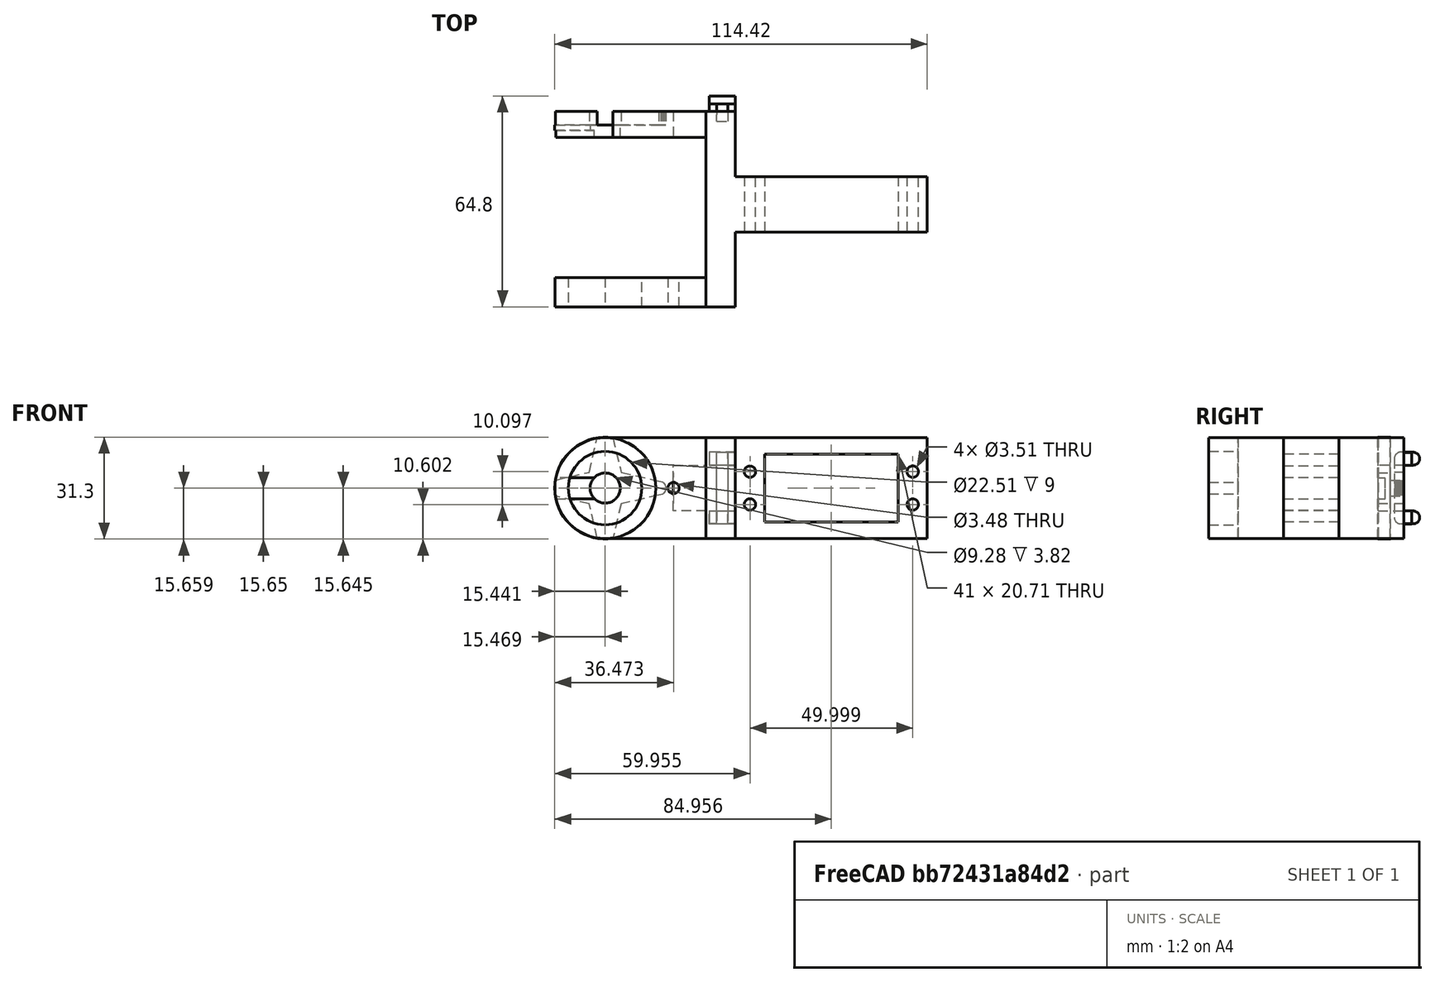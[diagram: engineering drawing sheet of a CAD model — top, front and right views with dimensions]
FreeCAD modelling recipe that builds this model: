
FCSTD DOCUMENT  (FreeCAD 1.0R38806 (Git))
Label: Eslabon_ajolote
License: All rights reserved
LicenseURL: https://en.wikipedia.org/wiki/All_rights_reserved
objects: Sketcher::SketchObject×17, TechDraw::DrawViewDimension×14, PartDesign::Pad×8, PartDesign::Pocket×8, PartDesign::Body×5, TechDraw::DrawProjGroupItem×5, PartDesign::ShapeBinder×4, PartDesign::Fillet×3, Part::MultiFuse×2, Part::Extrusion×1, Part::Fillet×1, TechDraw::DrawSVGTemplate×1, TechDraw::DrawProjGroup×1, TechDraw::DrawPage×1
note: 118 computed .brp shape members not serialized (recipe doc carries the construction recipe); baked Part::Feature solids carry a one-line shape summary decoded from their .brp

FEATURE [Sketcher::SketchObject] Sketch  label="rectángulo_atrás"
  ArcFitTolerance = 1e-06
  AttachmentSupport = -> [XY_Plane]
  FullyConstrained = false
  MakeInternals = false
  MapMode = 5
  sketch-geometry (4):
    g0: LineSegment StartX=94.9599 StartY=-16.0075 StartZ=0 EndX=35.9999 EndY=-16.0075 EndZ=0
    g1: LineSegment StartX=35.9999 StartY=-16.0075 StartZ=0 EndX=35.9999 EndY=-32.9967 EndZ=0
    g2: LineSegment StartX=35.9999 StartY=-32.9967 StartZ=0 EndX=94.9599 EndY=-32.9967 EndZ=0
    g3: LineSegment StartX=94.9599 StartY=-32.9967 StartZ=0 EndX=94.9599 EndY=-16.0075 EndZ=0
  constraints (8):
    c: Coincident(g0,g1)
    c: Coincident(g1,g2)
    c: Coincident(g2,g3)
    c: Coincident(g3,g0)
    c: Horizontal(g0)
    c: Horizontal(g2)
    c: Vertical(g1)
    c: Vertical(g3)
FEATURE [PartDesign::Pad] Pad  label="rectangulo_atras_extrusion"
  Direction = (0,0,1)
  Length = 31
  Length2 = 10
  Midplane = true
  Profile = -> Sketch
  ReferenceAxis = -> Sketch [N_Axis]
  Refine = true
  Suppressed = false
  Type = 0
FEATURE [Sketcher::SketchObject] Sketch001  label="orificios_parte_trasera"
  ArcFitTolerance = 1e-06
  AttachmentSupport = -> [Pad]
  FullyConstrained = false
  MakeInternals = false
  MapMode = 5
  Placement = pos=(0,-16.0075,0) rot=(0,0.707107,0.707107;3.14159rad)
  sketch-geometry (8):
    g0: LineSegment StartX=-85.9937 StartY=10.3574 StartZ=0 EndX=-85.9937 EndY=-10.3571 EndZ=0
    g1: LineSegment StartX=-85.9937 StartY=-10.3571 StartZ=0 EndX=-44.998 EndY=-10.3571 EndZ=0
    g2: LineSegment StartX=-44.998 StartY=-10.3571 StartZ=0 EndX=-44.998 EndY=10.3574 EndZ=0
    g3: LineSegment StartX=-44.998 StartY=10.3574 StartZ=0 EndX=-85.9937 EndY=10.3574 EndZ=0
    g4: Circle CenterX=-90.4933 CenterY=5.04829 CenterZ=0 NormalX=0 NormalY=0 NormalZ=1 AngleXU=0 Radius=1.75468
    g5: Circle CenterX=-90.4933 CenterY=-5.04829 CenterZ=0 NormalX=0 NormalY=0 NormalZ=1 AngleXU=0 Radius=1.75468
    g6: Circle CenterX=-40.4945 CenterY=5.04068 CenterZ=0 NormalX=0 NormalY=0 NormalZ=1 AngleXU=0 Radius=1.75279
    g7: Circle CenterX=-40.4945 CenterY=-5.04068 CenterZ=0 NormalX=0 NormalY=0 NormalZ=1 AngleXU=0 Radius=1.75279
  constraints (8):
    c: Coincident(g0,g1)
    c: Coincident(g1,g2)
    c: Coincident(g2,g3)
    c: Coincident(g3,g0)
    c: Vertical(g0)
    c: Vertical(g2)
    c: Horizontal(g1)
    c: Horizontal(g3)
FEATURE [PartDesign::Pocket] Pocket  label="rectangulo_atras_orificios"
  BaseFeature = -> Pad
  Direction = (0,-1,2e-16)
  Length = 4
  Length2 = 5
  Profile = -> Sketch001
  ReferenceAxis = -> Sketch001 [N_Axis]
  Refine = true
  Suppressed = false
  Type = 1
FEATURE [PartDesign::Body] Body  label="rectaángulo_de_atrás"
  AllowCompound = false
  Group = -> [Sketch,Pad,Sketch001,Pocket]
  Origin = -> Origin
  Tip = -> Pocket
FEATURE [Sketcher::SketchObject] Sketch002  label="rectangulo_vertical"
  ArcFitTolerance = 1e-06
  AttachmentSupport = -> [XY_Plane001]
  FullyConstrained = false
  MakeInternals = false
  MapMode = 5
  sketch-geometry (4):
    g0: LineSegment StartX=36 StartY=4 StartZ=0 EndX=27.0221 EndY=4 EndZ=0
    g1: LineSegment StartX=27.0221 StartY=4 StartZ=0 EndX=27.0221 EndY=-55.9831 EndZ=0
    g2: LineSegment StartX=27.0221 StartY=-55.9831 StartZ=0 EndX=36 EndY=-55.9831 EndZ=0
    g3: LineSegment StartX=36 StartY=-55.9831 StartZ=0 EndX=36 EndY=4 EndZ=0
  constraints (8):
    c: Coincident(g0,g1)
    c: Coincident(g1,g2)
    c: Coincident(g2,g3)
    c: Coincident(g3,g0)
    c: Horizontal(g0)
    c: Horizontal(g2)
    c: Vertical(g1)
    c: Vertical(g3)
FEATURE [PartDesign::Pad] Pad001
  Direction = (0,0,1)
  Length = 31
  Length2 = 10
  Midplane = true
  Profile = -> Sketch002
  ReferenceAxis = -> Sketch002 [N_Axis]
  Refine = true
  Suppressed = false
  Type = 0
FEATURE [Sketcher::SketchObject] Sketch003
  ArcFitTolerance = 1e-06
  AttachmentSupport = -> [Pad001]
  FullyConstrained = false
  MakeInternals = false
  MapMode = 5
  Placement = pos=(0,4,0) rot=(0,0.707107,0.707107;3.14159rad)
  sketch-geometry (4):
    g0: LineSegment StartX=-33.7559 StartY=-11.0015 StartZ=0 EndX=-30.2635 EndY=-11.0015 EndZ=0
    g1: LineSegment StartX=-30.2635 StartY=-11.0015 StartZ=0 EndX=-30.2635 EndY=11.0197 EndZ=0
    g2: LineSegment StartX=-30.2635 StartY=11.0197 StartZ=0 EndX=-33.7559 EndY=11.0197 EndZ=0
    g3: LineSegment StartX=-33.7559 StartY=11.0197 StartZ=0 EndX=-33.7559 EndY=-11.0015 EndZ=0
  constraints (8):
    c: Coincident(g0,g1)
    c: Coincident(g1,g2)
    c: Coincident(g2,g3)
    c: Coincident(g3,g0)
    c: Horizontal(g0)
    c: Horizontal(g2)
    c: Vertical(g1)
    c: Vertical(g3)
FEATURE [PartDesign::Pocket] Pocket001
  BaseFeature = -> Pad001
  Direction = (0,-1,2e-16)
  Length = 3
  Length2 = 5
  Profile = -> Sketch003
  ReferenceAxis = -> Sketch003 [N_Axis]
  Refine = true
  Suppressed = false
  Type = 0
FEATURE [PartDesign::Fillet] Fillet
  Base = -> Pocket001 [Edge24]
  BaseFeature = -> Pocket001
  Radius = 2
  Refine = true
  SupportTransform = false
  Suppressed = false
  UseAllEdges = false
FEATURE [PartDesign::Fillet] Fillet001
  Base = -> Fillet [Edge18]
  BaseFeature = -> Fillet
  Radius = 2
  Refine = true
  SupportTransform = false
  Suppressed = false
  UseAllEdges = false
FEATURE [Sketcher::SketchObject] Sketch004  label="base_arcos"
  ArcFitTolerance = 1e-06
  AttachmentSupport = -> [Fillet001]
  FullyConstrained = false
  MakeInternals = false
  MapMode = 5
  Placement = pos=(0,4,0) rot=(0,0.707107,0.707107;3.14159rad)
  sketch-geometry (16):
    g0: LineSegment StartX=-36.0015 StartY=-7.01539 StartZ=0 EndX=-36.0015 EndY=-10.9602 EndZ=0
    g1: LineSegment StartX=-36.0015 StartY=-10.9602 StartZ=0 EndX=-33.7554 EndY=-10.9602 EndZ=0
    g2: LineSegment StartX=-33.7554 StartY=-10.9602 StartZ=0 EndX=-33.7554 EndY=-7.01539 EndZ=0
    g3: LineSegment StartX=-33.7554 StartY=-7.01539 StartZ=0 EndX=-36.0015 EndY=-7.01539 EndZ=0
    g4: LineSegment StartX=-30.262 StartY=-10.9898 StartZ=0 EndX=-28.0069 EndY=-10.9898 EndZ=0
    g5: LineSegment StartX=-28.0069 StartY=-10.9898 StartZ=0 EndX=-28.0069 EndY=-7.03972 EndZ=0
    g6: LineSegment StartX=-28.0069 StartY=-7.03972 StartZ=0 EndX=-30.262 EndY=-7.03972 EndZ=0
    g7: LineSegment StartX=-30.262 StartY=-7.03972 StartZ=0 EndX=-30.262 EndY=-10.9898 EndZ=0
    g8: LineSegment StartX=-33.7554 StartY=7.01539 StartZ=0 EndX=-36.0015 EndY=7.01539 EndZ=0
    g9: LineSegment StartX=-36.0015 StartY=7.01539 StartZ=0 EndX=-36.0015 EndY=10.9602 EndZ=0
    g10: LineSegment StartX=-33.7554 StartY=10.9602 StartZ=0 EndX=-33.7554 EndY=7.01539 EndZ=0
    g11: LineSegment StartX=-36.0015 StartY=10.9602 StartZ=0 EndX=-33.7554 EndY=10.9602 EndZ=0
    g12: LineSegment StartX=-30.262 StartY=7.03972 StartZ=0 EndX=-30.262 EndY=10.9898 EndZ=0
    g13: LineSegment StartX=-30.262 StartY=10.9898 StartZ=0 EndX=-28.0069 EndY=10.9898 EndZ=0
    g14: LineSegment StartX=-28.0069 StartY=10.9898 StartZ=0 EndX=-28.0069 EndY=7.03972 EndZ=0
    g15: LineSegment StartX=-28.0069 StartY=7.03972 StartZ=0 EndX=-30.262 EndY=7.03972 EndZ=0
  constraints (32):
    c: Coincident(g0,g1)
    c: Coincident(g1,g2)
    c: Coincident(g2,g3)
    c: Coincident(g3,g0)
    c: Vertical(g0)
    c: Vertical(g2)
    c: Horizontal(g1)
    c: Horizontal(g3)
    c: Coincident(g4,g5)
    c: Coincident(g5,g6)
    c: Coincident(g6,g7)
    c: Coincident(g7,g4)
    c: Horizontal(g4)
    c: Horizontal(g6)
    c: Vertical(g5)
    c: Vertical(g7)
    c: Coincident(g9,g11)
    c: Coincident(g11,g10)
    c: Coincident(g10,g8)
    c: Coincident(g8,g9)
    c: Vertical(g9)
    c: Vertical(g10)
    c: Horizontal(g11)
    c: Horizontal(g8)
    c: Coincident(g13,g14)
    c: Coincident(g14,g15)
    c: Coincident(g15,g12)
    c: Coincident(g12,g13)
    c: Horizontal(g13)
    c: Horizontal(g15)
    c: Vertical(g14)
    c: Vertical(g12)
FEATURE [PartDesign::Pad] Pad002
  BaseFeature = -> Fillet001
  Direction = (0,1,-2e-16)
  Length = 2.3
  Length2 = 10
  Profile = -> Sketch004
  ReferenceAxis = -> Sketch004 [N_Axis]
  Refine = true
  Suppressed = false
  Type = 0
FEATURE [PartDesign::Body] Body001  label="rectángulo_vertical"
  AllowCompound = false
  Group = -> [Sketch002,Pad001,Sketch003,Pocket001,Fillet,Fillet001,Sketch004,Pad002]
  Origin = -> Origin001
  Tip = -> Pad002
FEATURE [PartDesign::ShapeBinder] CopyPad002
  TraceSupport = false
FEATURE [Sketcher::SketchObject] Sketch005  label="arco1"
  ArcFitTolerance = 1e-06
  AttachmentSupport = -> [CopyPad002]
  FullyConstrained = false
  MakeInternals = false
  MapMode = 5
  Placement = pos=(28.0069,0,0) rot=(0.57735,-0.57735,-0.57735;2.0944rad)
  sketch-geometry (4):
    g0: LineSegment StartX=-6.29983 StartY=-10.98 StartZ=0 EndX=-6.29983 EndY=-7.03975 EndZ=0
    g1: LineSegment StartX=-6.29983 StartY=-7.03975 StartZ=0 EndX=-8.80088 EndY=-7.03975 EndZ=0
    g2: LineSegment StartX=-8.80088 StartY=-7.03975 StartZ=0 EndX=-8.80088 EndY=-10.98 EndZ=0
    g3: LineSegment StartX=-8.80088 StartY=-10.98 StartZ=0 EndX=-6.29983 EndY=-10.98 EndZ=0
  constraints (8):
    c: Coincident(g1,g2)
    c: Coincident(g2,g3)
    c: Coincident(g3,g0)
    c: Coincident(g0,g1)
    c: Horizontal(g1)
    c: Horizontal(g3)
    c: Vertical(g2)
    c: Vertical(g0)
FEATURE [PartDesign::Pad] Pad003
  Direction = (-1,0,0)
  Length = 8
  Length2 = 10
  Profile = -> Sketch005
  ReferenceAxis = -> Sketch005 [N_Axis]
  Refine = true
  Reversed = true
  Suppressed = false
  Type = 0
FEATURE [PartDesign::Fillet] Fillet002
  Base = -> Pad003 [Edge5,Edge8]
  BaseFeature = -> Pad003
  Radius = 1.97
  Refine = true
  SupportTransform = false
  Suppressed = false
  UseAllEdges = false
FEATURE [PartDesign::ShapeBinder] CopyPad003
  TraceSupport = false
FEATURE [Sketcher::SketchObject] Sketch006
  ArcFitTolerance = 1e-06
  AttachmentSupport = -> [CopyPad003]
  FullyConstrained = false
  MakeInternals = false
  MapMode = 5
  Placement = pos=(28.0069,0,0) rot=(0.57735,-0.57735,-0.57735;2.0944rad)
  sketch-geometry (4):
    g0: LineSegment StartX=-6.29941 StartY=10.9899 StartZ=0 EndX=-8.79941 EndY=10.9899 EndZ=0
    g1: LineSegment StartX=-8.79941 StartY=10.9899 StartZ=0 EndX=-8.79941 EndY=7.04044 EndZ=0
    g2: LineSegment StartX=-8.79941 StartY=7.04044 StartZ=0 EndX=-6.29941 EndY=7.04044 EndZ=0
    g3: LineSegment StartX=-6.29941 StartY=7.04044 StartZ=0 EndX=-6.29941 EndY=10.9899 EndZ=0
  constraints (9):
    c: Coincident(g0,g1)
    c: Coincident(g1,g2)
    c: Coincident(g2,g3)
    c: Coincident(g3,g0)
    c: Horizontal(g0)
    c: Horizontal(g2)
    c: Vertical(g1)
    c: Vertical(g3)
    c: Distance(g2,g2) = 2.5
FEATURE [PartDesign::Body] Body002  label="arcos_rect_vertical"
  AllowCompound = false
  Group = -> [CopyPad002,Sketch005,Pad003,Fillet002,CopyPad003,Sketch006]
  Origin = -> Origin002
  Tip = -> Fillet002
FEATURE [Part::Extrusion] Extrude
  Base = -> Sketch006
  Dir = (-1,0,0)
  DirMode = 2
  FaceMakerClass = Part::FaceMakerBullseye
  FaceMakerMode = 3
  LengthFwd = 8
  LengthRev = 0
  Placement = pos=(8.02,0,0) rot=(0,0,1;0rad)
  Solid = true
  Symmetric = false
FEATURE [Part::Fillet] Fillet003
  Base = -> Extrude
  EdgeLinks = -> Extrude [Edge2,Edge5]
  Edges = 2 edges r=1.97: [Edge2,Edge5]
FEATURE [PartDesign::ShapeBinder] CopyPad004
  TraceSupport = false
FEATURE [Sketcher::SketchObject] Sketch007
  ArcFitTolerance = 1e-06
  AttachmentSupport = -> [CopyPad004]
  FullyConstrained = false
  MakeInternals = false
  MapMode = 5
  Placement = pos=(27.0221,0,0) rot=(0.57735,-0.57735,-0.57735;2.0944rad)
  sketch-geometry (4):
    g0: LineSegment StartX=3.99643 StartY=-15.4941 StartZ=0 EndX=3.99643 EndY=15.498 EndZ=0
    g1: LineSegment StartX=3.99643 StartY=15.498 StartZ=0 EndX=-3.99801 EndY=15.498 EndZ=0
    g2: LineSegment StartX=-3.99801 StartY=15.498 StartZ=0 EndX=-3.99801 EndY=-15.4941 EndZ=0
    g3: LineSegment StartX=-3.99801 StartY=-15.4941 StartZ=0 EndX=3.99643 EndY=-15.4941 EndZ=0
  constraints (8):
    c: Coincident(g0,g1)
    c: Coincident(g1,g2)
    c: Coincident(g2,g3)
    c: Coincident(g3,g0)
    c: Vertical(g0)
    c: Vertical(g2)
    c: Horizontal(g1)
    c: Horizontal(g3)
FEATURE [PartDesign::Pad] Pad004
  Direction = (-1,0,0)
  Length = 28.65
  Length2 = 10
  Profile = -> Sketch007
  ReferenceAxis = -> Sketch007 [N_Axis]
  Refine = true
  Suppressed = false
  Type = 0
FEATURE [Sketcher::SketchObject] Sketch008
  ArcFitTolerance = 1e-06
  AttachmentSupport = -> [Pad004]
  FullyConstrained = false
  MakeInternals = false
  MapMode = 5
  Placement = pos=(0,3.99801,0) rot=(0,0.707107,0.707107;3.14159rad)
  sketch-geometry (1):
    g0: Circle CenterX=3.81574 CenterY=0.001435 CenterZ=0 NormalX=0 NormalY=0 NormalZ=1 AngleXU=0 Radius=15.649
FEATURE [PartDesign::Pad] Pad005
  BaseFeature = -> Pad004
  Direction = (0,1,-2e-16)
  Length = 8
  Length2 = 10
  Profile = -> Sketch008
  ReferenceAxis = -> Sketch008 [N_Axis]
  Refine = true
  Reversed = true
  Suppressed = false
  Type = 0
FEATURE [Sketcher::SketchObject] Sketch009
  ArcFitTolerance = 1e-06
  AttachmentSupport = -> [Pad005]
  FullyConstrained = false
  MakeInternals = false
  MapMode = 5
  Placement = pos=(0,3.998,0) rot=(0,0.707107,0.707107;3.14159rad)
  sketch-geometry (4):
    g0: LineSegment StartX=-27.0232 StartY=6.99906 StartZ=0 EndX=-27.0232 EndY=-7 EndZ=0
    g1: LineSegment StartX=-27.0232 StartY=-7 StartZ=0 EndX=-17 EndY=-7 EndZ=0
    g2: LineSegment StartX=-17 StartY=-7 StartZ=0 EndX=-17 EndY=6.99906 EndZ=0
    g3: LineSegment StartX=-17 StartY=6.99906 StartZ=0 EndX=-27.0232 EndY=6.99906 EndZ=0
  constraints (8):
    c: Coincident(g0,g1)
    c: Coincident(g1,g2)
    c: Coincident(g2,g3)
    c: Coincident(g3,g0)
    c: Vertical(g0)
    c: Vertical(g2)
    c: Horizontal(g1)
    c: Horizontal(g3)
FEATURE [PartDesign::Pocket] Pocket002
  BaseFeature = -> Pad005
  Direction = (0,-1,2e-16)
  Length = 5
  Length2 = 5
  Profile = -> Sketch009
  ReferenceAxis = -> Sketch009 [N_Axis]
  Refine = true
  Suppressed = false
  Type = 1
FEATURE [Sketcher::SketchObject] Sketch010  label="pieza_motor"
  ArcFitTolerance = 1e-06
  AttachmentSupport = -> [Pocket002]
  FullyConstrained = false
  MakeInternals = false
  MapMode = 5
  Placement = pos=(0,3.998,0) rot=(0,0.707107,0.707107;3.14159rad)
  sketch-geometry (28):
    g0: LineSegment StartX=-0.879047 StartY=4.87904 StartZ=0 EndX=-12.5 EndY=2.15 EndZ=0
    g1: LineSegment StartX=-12.5 StartY=2.15 StartZ=0 EndX=-13.0565 EndY=2.07674 EndZ=0
    g2: LineSegment StartX=-13.0565 StartY=2.07674 StartZ=0 EndX=-13.575 EndY=1.86195 EndZ=0
    g3: LineSegment StartX=-13.575 StartY=1.86195 StartZ=0 EndX=-14.0206 EndY=1.5196 EndZ=0
    g4: LineSegment StartX=-14.0206 StartY=1.5196 StartZ=0 EndX=-14.3615 EndY=1.07502 EndZ=0
    g5: LineSegment StartX=-14.3615 StartY=1.07502 StartZ=0 EndX=-14.577 EndY=0.55653 EndZ=0
    g6: LineSegment StartX=-14.577 StartY=0.55653 StartZ=0 EndX=-14.65 EndY=0 EndZ=0
    g7: LineSegment StartX=-14.65 StartY=0 StartZ=0 EndX=-14.5764 EndY=-0.556616 EndZ=0
    g8: LineSegment StartX=-14.5764 StartY=-0.556616 StartZ=0 EndX=-14.3614 EndY=-1.07512 EndZ=0
    g9: LineSegment StartX=-14.3614 StartY=-1.07512 StartZ=0 EndX=-14.0193 EndY=-1.51973 EndZ=0
    g10: LineSegment StartX=-14.0193 StartY=-1.51973 StartZ=0 EndX=-13.5752 EndY=-1.8617 EndZ=0
    g11: LineSegment StartX=-13.5752 StartY=-1.8617 StartZ=0 EndX=-13.0567 EndY=-2.07653 EndZ=0
    g12: LineSegment StartX=-13.0567 StartY=-2.07653 StartZ=0 EndX=-12.5005 EndY=-2.14944 EndZ=0
    g13: LineSegment StartX=-12.5005 StartY=-2.14944 StartZ=0 EndX=-0.879091 EndY=-4.87901 EndZ=0
    g14: LineSegment StartX=-0.879091 StartY=-4.87901 StartZ=0 EndX=1.6565 EndY=-15.671 EndZ=0
    g15: LineSegment StartX=1.6565 StartY=-15.671 StartZ=0 EndX=4.61301 EndY=-15.8475 EndZ=0
    g16: LineSegment StartX=4.61301 StartY=-15.8475 StartZ=0 EndX=6.39034 EndY=-15.5456 EndZ=0
    g17: LineSegment StartX=6.39034 StartY=-15.5456 StartZ=0 EndX=8.87904 EndY=-4.87904 EndZ=0
    g18: LineSegment StartX=8.87904 StartY=-4.87904 StartZ=0 EndX=19.2921 EndY=-2.46566 EndZ=0
    g19: LineSegment StartX=19.2921 StartY=-2.46566 StartZ=0 EndX=19.4511 EndY=-1.24638 EndZ=0
    g20: LineSegment StartX=19.4511 StartY=-1.24638 StartZ=0 EndX=19.4973 EndY=-0.017855 EndZ=0
    g21: LineSegment StartX=19.4973 StartY=-0.017855 StartZ=0 EndX=19.4476 EndY=1.21172 EndZ=0
    g22: LineSegment StartX=19.4476 StartY=1.21172 StartZ=0 EndX=19.3061 EndY=2.42886 EndZ=0
    g23: LineSegment StartX=19.3061 StartY=2.42886 StartZ=0 EndX=8.87901 EndY=4.87903 EndZ=0
    g24: LineSegment StartX=8.87901 StartY=4.87903 StartZ=0 EndX=6.40298 EndY=15.4805 EndZ=0
    g25: LineSegment StartX=6.40298 StartY=15.4805 StartZ=0 EndX=4.6357 EndY=15.8006 EndZ=0
    g26: LineSegment StartX=4.6357 StartY=15.8006 StartZ=0 EndX=1.61602 EndY=15.6057 EndZ=0
    g27: LineSegment StartX=1.61602 StartY=15.6057 StartZ=0 EndX=-0.879047 EndY=4.87904 EndZ=0
  constraints (29):
    c: Coincident(g0,g1)
    c: Coincident(g1,g2)
    c: Coincident(g2,g3)
    c: Coincident(g3,g4)
    c: Coincident(g4,g5)
    c: Coincident(g5,g6)
    c: PointOnObject(g6,g-1)
    c: Coincident(g6,g7)
    c: Coincident(g7,g8)
    c: Coincident(g8,g9)
    c: Coincident(g9,g10)
    c: Coincident(g10,g11)
    c: Coincident(g11,g12)
    c: Coincident(g12,g13)
    c: Coincident(g13,g14)
    c: Coincident(g14,g15)
    c: Coincident(g15,g16)
    c: Coincident(g16,g17)
    c: Coincident(g17,g18)
    c: Coincident(g18,g19)
    c: Coincident(g19,g20)
    c: Coincident(g20,g21)
    c: Coincident(g21,g22)
    c: Coincident(g22,g23)
    c: Coincident(g23,g24)
    c: Coincident(g24,g25)
    c: Coincident(g25,g26)
    c: Coincident(g26,g27)
    c: Coincident(g27,g0)
FEATURE [PartDesign::Pocket] Pocket003
  BaseFeature = -> Pocket002
  Direction = (0,-1,2e-16)
  Length = 4.18
  Length2 = 5
  Profile = -> Sketch010
  ReferenceAxis = -> Sketch010 [N_Axis]
  Refine = true
  Suppressed = false
  Type = 0
FEATURE [Sketcher::SketchObject] Sketch011  label="circulo_motor"
  ArcFitTolerance = 1e-06
  AttachmentSupport = -> [Pocket003]
  FullyConstrained = false
  MakeInternals = false
  MapMode = 5
  Placement = pos=(0,-0.181995,0) rot=(0,0.707107,0.707107;3.14159rad)
  sketch-geometry (1):
    g0: Circle CenterX=3.99101 CenterY=0 CenterZ=0 NormalX=0 NormalY=0 NormalZ=1 AngleXU=0 Radius=4.64163
FEATURE [PartDesign::Pocket] Pocket004
  BaseFeature = -> Pocket003
  Direction = (0,-1,2e-16)
  Length = 5
  Length2 = 5
  Profile = -> Sketch011
  ReferenceAxis = -> Sketch011 [N_Axis]
  Refine = true
  Suppressed = false
  Type = 0
FEATURE [PartDesign::ShapeBinder] CopyPad005
  TraceSupport = false
FEATURE [Sketcher::SketchObject] Sketch012  label="parte_abajo"
  ArcFitTolerance = 1e-06
  AttachmentSupport = -> [CopyPad005]
  FullyConstrained = false
  MakeInternals = false
  MapMode = 5
  Placement = pos=(27.0221,0,0) rot=(0.57735,-0.57735,-0.57735;2.0944rad)
  sketch-geometry (4):
    g0: LineSegment StartX=46.9997 StartY=-15.5 StartZ=0 EndX=55.9806 EndY=-15.5 EndZ=0
    g1: LineSegment StartX=55.9806 StartY=-15.5 StartZ=0 EndX=55.9806 EndY=15.4935 EndZ=0
    g2: LineSegment StartX=55.9806 StartY=15.4935 StartZ=0 EndX=46.9997 EndY=15.4935 EndZ=0
    g3: LineSegment StartX=46.9997 StartY=15.4935 StartZ=0 EndX=46.9997 EndY=-15.5 EndZ=0
  constraints (8):
    c: Coincident(g0,g1)
    c: Coincident(g1,g2)
    c: Coincident(g2,g3)
    c: Coincident(g3,g0)
    c: Horizontal(g0)
    c: Horizontal(g2)
    c: Vertical(g1)
    c: Vertical(g3)
FEATURE [PartDesign::Pad] Pad006
  Direction = (-1,0,0)
  Length = 31
  Length2 = 10
  Profile = -> Sketch012
  ReferenceAxis = -> Sketch012 [N_Axis]
  Refine = true
  Suppressed = false
  Type = 0
FEATURE [Sketcher::SketchObject] Sketch013
  ArcFitTolerance = 1e-06
  AttachmentSupport = -> [Pad006]
  FullyConstrained = false
  MakeInternals = false
  MapMode = 5
  Placement = pos=(0,-46.9997,0) rot=(0,0.707107,0.707107;3.14159rad)
  sketch-geometry (1):
    g0: Circle CenterX=3.93139 CenterY=-0.003132 CenterZ=0 NormalX=0 NormalY=0 NormalZ=1 AngleXU=0 Radius=15.4968
FEATURE [PartDesign::Pad] Pad007
  BaseFeature = -> Pad006
  Direction = (0,1,-2e-16)
  Length = 9
  Length2 = 10
  Profile = -> Sketch013
  ReferenceAxis = -> Sketch013 [N_Axis]
  Refine = true
  Reversed = true
  Suppressed = false
  Type = 0
FEATURE [Sketcher::SketchObject] Sketch014
  ArcFitTolerance = 1e-06
  AttachmentSupport = -> [Pad007]
  FullyConstrained = false
  MakeInternals = false
  MapMode = 5
  Placement = pos=(0,-46.9997,0) rot=(0,0.707107,0.707107;3.14159rad)
  sketch-geometry (1):
    g0: Circle CenterX=4.01934 CenterY=-0.005181 CenterZ=0 NormalX=0 NormalY=0 NormalZ=1 AngleXU=0 Radius=11.2566
FEATURE [PartDesign::Pocket] Pocket005
  BaseFeature = -> Pad007
  Direction = (0,-1,2e-16)
  Length = 5
  Length2 = 5
  Profile = -> Sketch014
  ReferenceAxis = -> Sketch014 [N_Axis]
  Refine = true
  Suppressed = false
  Type = 1
FEATURE [Sketcher::SketchObject] Sketch015
  ArcFitTolerance = 1e-06
  AttachmentSupport = -> [Pocket005]
  FullyConstrained = false
  MakeInternals = false
  MapMode = 5
  Placement = pos=(0,-46.9997,0) rot=(0,0.707107,0.707107;3.14159rad)
  sketch-geometry (1):
    g0: Circle CenterX=-17.0133 CenterY=0.008823 CenterZ=0 NormalX=0 NormalY=0 NormalZ=1 AngleXU=0 Radius=1.74011
FEATURE [PartDesign::Pocket] Pocket006
  BaseFeature = -> Pocket005
  Direction = (0,-1,2e-16)
  Length = 5
  Length2 = 5
  Profile = -> Sketch015
  ReferenceAxis = -> Sketch015 [N_Axis]
  Refine = true
  Suppressed = false
  Type = 1
FEATURE [PartDesign::Body] Body004  label="parte_abajo_motor"
  AllowCompound = false
  Group = -> [CopyPad005,Sketch012,Pad006,Sketch013,Pad007,Sketch014,Pocket005,Sketch015,Pocket006]
  Origin = -> Origin004
  Tip = -> Pocket006
FEATURE [Sketcher::SketchObject] Sketch016
  ArcFitTolerance = 1e-06
  AttachmentSupport = -> [Pocket004]
  FullyConstrained = false
  MakeInternals = false
  MapMode = 5
  Placement = pos=(0,-4.00199,9e-16) rot=(1,0,0;1.5708rad)
  sketch-geometry (10):
    g0: LineSegment StartX=-19.2748 StartY=3.22908 StartZ=0 EndX=-19.699 EndY=0 EndZ=0
    g1: LineSegment StartX=-19.699 StartY=0 StartZ=0 EndX=-19.3234 EndY=-3.25533 EndZ=0
    g2: LineSegment StartX=-19.3234 StartY=-3.25533 StartZ=0 EndX=-6.56478 EndY=-3.25533 EndZ=0
    g3: LineSegment StartX=-6.56478 StartY=-3.25533 StartZ=0 EndX=-7.50808 EndY=-1.87562 EndZ=0
    g4: LineSegment StartX=-7.50808 StartY=-1.87562 StartZ=0 EndX=-7.78613 EndY=-0.643242 EndZ=0
    g5: LineSegment StartX=-7.78613 StartY=-0.643242 StartZ=0 EndX=-7.89265 EndY=0.261497 EndZ=0
    g6: LineSegment StartX=-7.89265 StartY=0.261497 StartZ=0 EndX=-7.60646 EndY=1.23701 EndZ=0
    g7: LineSegment StartX=-7.60646 StartY=1.23701 StartZ=0 EndX=-7.38775 EndY=2.24473 EndZ=0
    g8: LineSegment StartX=-7.38775 StartY=2.24473 StartZ=0 EndX=-6.50057 EndY=3.22908 EndZ=0
    g9: LineSegment StartX=-6.50057 StartY=3.22908 StartZ=0 EndX=-19.2748 EndY=3.22908 EndZ=0
  constraints (13):
    c: PointOnObject(g0,g-1)
    c: Coincident(g0,g1)
    c: Coincident(g1,g2)
    c: Horizontal(g2)
    c: Coincident(g2,g3)
    c: Coincident(g3,g4)
    c: Coincident(g4,g5)
    c: Coincident(g5,g6)
    c: Coincident(g6,g7)
    c: Coincident(g7,g8)
    c: Coincident(g8,g9)
    c: Coincident(g9,g0)
    c: Horizontal(g9)
FEATURE [PartDesign::Pocket] Pocket007
  BaseFeature = -> Pocket004
  Direction = (0,1,-2e-16)
  Length = 2.2
  Length2 = 5
  Profile = -> Sketch016
  ReferenceAxis = -> Sketch016 [N_Axis]
  Refine = true
  Suppressed = false
  Type = 0
FEATURE [PartDesign::Body] Body003  label="parte_arriba_motor"
  AllowCompound = false
  Group = -> [CopyPad004,Sketch007,Pad004,Sketch008,Pad005,Sketch009,Pocket002,Sketch010,Pocket003,Sketch011,Pocket004,Sketch016,Pocket007]
  Origin = -> Origin003
  Tip = -> Pocket007
FEATURE [Part::MultiFuse] Fusion  label="arcos"
  Refine = true
  Shapes = -> [Body002,Fillet003]
FEATURE [Part::MultiFuse] Fusion001  label="eslabón"
  Refine = true
  Shapes = -> [Body,Body001,Body003,Body004,Fusion]
FEATURE [TechDraw::DrawSVGTemplate] Template
  EditableTexts = approval_person=Mecatrónica; creator=A.Mrtz, N.Grc, T.Marí; date_of_issue=12/14/24; document_status=In preparation; document_type=Eslabon_ajolote; drawing_number=DN; general_tolerances=ISO 2768-m; language_code=EN; part_material=Stainless steel Mat.No. 1.4301; responsible_department=RD; revision_index=AAA; sheet_number=1 / 1; sheet_scale=1 : 1; title=Eslabon_ajolote
  Height = 297
  Orientation = 1
  Template = <path>
  Width = 420
FEATURE [TechDraw::DrawProjGroupItem] ProjItem  label="Front"
  CoarseView = false
  Direction = (0,0,-1)
  Focus = 100
  HardHidden = false
  IsoCount = 0
  IsoHidden = false
  IsoVisible = false
  LockPosition = true
  Perspective = false
  Rotation = 0
  RotationVector = (-1,0,0)
  ScaleType = 0
  ScrubCount = 1
  SeamHidden = false
  SeamVisible = false
  SmoothHidden = false
  SmoothVisible = true
  Source = -> [Fusion001]
  Type = 0
  X = 0
  XDirection = (-1,0,0)
  Y = 0
FEATURE [TechDraw::DrawProjGroupItem] ProjItem001  label="Top"
  CoarseView = false
  Direction = (0,1,0)
  Focus = 100
  HardHidden = false
  IsoCount = 0
  IsoHidden = false
  IsoVisible = false
  LockPosition = false
  Perspective = false
  Rotation = 0
  RotationVector = (1,0,0)
  ScaleType = 0
  ScrubCount = 1
  SeamHidden = false
  SeamVisible = false
  SmoothHidden = false
  SmoothVisible = true
  Source = -> [Fusion001]
  Type = 4
  X = 0
  XDirection = (-1,0,0)
  Y = -91.5512
FEATURE [TechDraw::DrawProjGroupItem] ProjItem002  label="Left"
  CoarseView = false
  Direction = (1,0,-1e-16)
  Focus = 100
  HardHidden = false
  IsoCount = 0
  IsoHidden = false
  IsoVisible = false
  LockPosition = false
  Perspective = false
  Rotation = 0
  RotationVector = (1,0,0)
  ScaleType = 0
  ScrubCount = 1
  SeamHidden = false
  SeamVisible = false
  SmoothHidden = false
  SmoothVisible = true
  Source = -> [Fusion001]
  Type = 1
  X = 87.8613
  XDirection = (-1e-16,0,-1)
  Y = 0
FEATURE [TechDraw::DrawProjGroupItem] ProjItem003  label="FrontTopRight"
  CoarseView = false
  Direction = (-0.57735,0.57735,-0.57735)
  Focus = 100
  HardHidden = false
  IsoCount = 0
  IsoHidden = false
  IsoVisible = false
  LockPosition = false
  Perspective = false
  Rotation = 0
  RotationVector = (1,0,0)
  ScaleType = 0
  ScrubCount = 1
  SeamHidden = false
  SeamVisible = false
  SmoothHidden = false
  SmoothVisible = true
  Source = -> [Fusion001]
  Type = 7
  X = 200.056
  XDirection = (-0.707107,0,0.707107)
  Y = -2.23864
FEATURE [TechDraw::DrawViewDimension] Dimension
  AngleOverride = false
  Arbitrary = false
  ArbitraryTolerances = false
  BoxCorners = (2) [(-57.2123,-32.4003,-1e-07),(57.2123,32.4003,1e-07)]
  EqualTolerance = true
  ExtensionAngle = 0
  FormatSpec = %.2w
  FormatSpecOverTolerance = %+.2w
  FormatSpecUnderTolerance = %+.2w
  Inverted = false
  LineAngle = 0
  LockPosition = false
  MeasureType = 1
  OverTolerance = 0
  References2D = -> [ProjItem]
  Rotation = 0
  ScaleType = 0
  TheoreticalExact = false
  Type = 1
  UnderTolerance = 0
  X = -27.7324
  Y = -43.1155
FEATURE [TechDraw::DrawViewDimension] Dimension001
  AngleOverride = false
  Arbitrary = false
  ArbitraryTolerances = false
  BoxCorners = (2) [(-57.2123,-32.4003,-1e-07),(57.2123,32.4003,1e-07)]
  EqualTolerance = true
  ExtensionAngle = 0
  FormatSpec = %.2w
  FormatSpecOverTolerance = %+.2w
  FormatSpecUnderTolerance = %+.2w
  Inverted = false
  LineAngle = 0
  LockPosition = false
  MeasureType = 1
  OverTolerance = 0
  References2D = -> [ProjItem]
  Rotation = 0
  ScaleType = 0
  TheoreticalExact = false
  Type = 0
  UnderTolerance = 0
  X = -81.8359
  Y = -26.9436
FEATURE [TechDraw::DrawViewDimension] Dimension002
  AngleOverride = false
  Arbitrary = false
  ArbitraryTolerances = false
  BoxCorners = (2) [(-57.2123,-32.4003,-1e-07),(57.2123,32.4003,1e-07)]
  EqualTolerance = true
  ExtensionAngle = 0
  FormatSpec = %.2w
  FormatSpecOverTolerance = %+.2w
  FormatSpecUnderTolerance = %+.2w
  Inverted = false
  LineAngle = 0
  LockPosition = false
  MeasureType = 1
  OverTolerance = 0
  References2D = -> [ProjItem]
  Rotation = 0
  ScaleType = 0
  TheoreticalExact = false
  Type = 0
  UnderTolerance = 0
  X = 58.4563
  Y = 37.7437
FEATURE [TechDraw::DrawViewDimension] Dimension003
  AngleOverride = false
  Arbitrary = false
  ArbitraryTolerances = false
  BoxCorners = (2) [(-57.2123,-32.4003,-1e-07),(57.2123,32.4003,1e-07)]
  EqualTolerance = true
  ExtensionAngle = 0
  FormatSpec = %.2w
  FormatSpecOverTolerance = %+.2w
  FormatSpecUnderTolerance = %+.2w
  Inverted = false
  LineAngle = 0
  LockPosition = false
  MeasureType = 1
  OverTolerance = 0
  References2D = -> [ProjItem]
  Rotation = 0
  ScaleType = 0
  TheoreticalExact = false
  Type = 0
  UnderTolerance = 0
  X = 58.4563
  Y = -44.2181
FEATURE [TechDraw::DrawViewDimension] Dimension004
  AngleOverride = false
  Arbitrary = false
  ArbitraryTolerances = false
  BoxCorners = (2) [(-57.2123,-15.649,-1e-07),(57.2123,15.649,1e-07)]
  EqualTolerance = true
  ExtensionAngle = 0
  FormatSpec = %.2w
  FormatSpecOverTolerance = %+.2w
  FormatSpecUnderTolerance = %+.2w
  Inverted = false
  LineAngle = 0
  LockPosition = false
  MeasureType = 1
  OverTolerance = 0
  References2D = -> [ProjItem001]
  Rotation = 0
  ScaleType = 0
  TheoreticalExact = false
  Type = 1
  UnderTolerance = 0
  X = -27.7483
  Y = -29.1155
FEATURE [TechDraw::DrawViewDimension] Dimension005
  AngleOverride = false
  Arbitrary = false
  ArbitraryTolerances = false
  BoxCorners = (2) [(-57.2123,-15.649,-1e-07),(57.2123,15.649,1e-07)]
  EqualTolerance = true
  ExtensionAngle = 0
  FormatSpec = R%.2w
  FormatSpecOverTolerance = %+.2w
  FormatSpecUnderTolerance = %+.2w
  Inverted = false
  LineAngle = 0
  LockPosition = false
  MeasureType = 1
  OverTolerance = 0
  References2D = -> [ProjItem001]
  Rotation = 0
  ScaleType = 0
  TheoreticalExact = false
  Type = 4
  UnderTolerance = 0
  X = -79.389
  Y = -5.88066
FEATURE [TechDraw::DrawViewDimension] Dimension006
  AngleOverride = false
  Arbitrary = false
  ArbitraryTolerances = false
  BoxCorners = (2) [(-57.2123,-15.649,-1e-07),(57.2123,15.649,1e-07)]
  EqualTolerance = true
  ExtensionAngle = 0
  FormatSpec = R%.2w
  FormatSpecOverTolerance = %+.2w
  FormatSpecUnderTolerance = %+.2w
  Inverted = false
  LineAngle = 0
  LockPosition = false
  MeasureType = 1
  OverTolerance = 0
  References2D = -> [ProjItem001]
  Rotation = 0
  ScaleType = 0
  TheoreticalExact = false
  Type = 4
  UnderTolerance = 0
  X = 72.0381
  Y = -5.14558
FEATURE [TechDraw::DrawProjGroupItem] ProjItem004  label="Bottom"
  CoarseView = false
  Direction = (0,-1,0)
  Focus = 100
  HardHidden = false
  IsoCount = 0
  IsoHidden = false
  IsoVisible = false
  LockPosition = false
  Perspective = false
  Rotation = 0
  RotationVector = (1,0,0)
  ScaleType = 0
  ScrubCount = 1
  SeamHidden = false
  SeamVisible = false
  SmoothHidden = false
  SmoothVisible = true
  Source = -> [Fusion001]
  Type = 5
  X = 0
  XDirection = (-1,0,0)
  Y = 63.0493
FEATURE [TechDraw::DrawProjGroup] ProjGroup
  Anchor = -> ProjItem
  AutoDistribute = true
  LockPosition = false
  ProjectionType = 0
  Rotation = 0
  ScaleType = 0
  Source = -> [Fusion001]
  Views = -> [ProjItem,ProjItem001,ProjItem002,ProjItem003,ProjItem004]
  X = 129.876
  Y = 178.271
  spacingX = 15
  spacingY = 15
FEATURE [TechDraw::DrawViewDimension] Dimension007
  AngleOverride = false
  Arbitrary = false
  ArbitraryTolerances = false
  BoxCorners = (2) [(-57.2123,-15.649,0),(57.2123,15.649,0)]
  EqualTolerance = true
  ExtensionAngle = 0
  FormatSpec = ⌀%.2w
  FormatSpecOverTolerance = %+.2w
  FormatSpecUnderTolerance = %+.2w
  Inverted = false
  LineAngle = 0
  LockPosition = false
  MeasureType = 1
  OverTolerance = 0
  References2D = -> [ProjItem004]
  Rotation = 0
  ScaleType = 0
  TheoreticalExact = false
  Type = 5
  UnderTolerance = 0
  X = 22.7876
  Y = 30.5059
FEATURE [TechDraw::DrawViewDimension] Dimension008
  AngleOverride = false
  Arbitrary = false
  ArbitraryTolerances = false
  BoxCorners = (2) [(-57.2123,-15.649,0),(57.2123,15.649,0)]
  EqualTolerance = true
  ExtensionAngle = 0
  FormatSpec = R%.2w
  FormatSpecOverTolerance = %+.2w
  FormatSpecUnderTolerance = %+.2w
  Inverted = false
  LineAngle = 0
  LockPosition = false
  MeasureType = 1
  OverTolerance = 0
  References2D = -> [ProjItem004]
  Rotation = 0
  ScaleType = 0
  TheoreticalExact = false
  Type = 4
  UnderTolerance = 0
  X = 44.8401
  Y = 27.9332
FEATURE [TechDraw::DrawViewDimension] Dimension009
  AngleOverride = false
  Arbitrary = false
  ArbitraryTolerances = false
  BoxCorners = (2) [(-57.2123,-15.649,0),(57.2123,15.649,0)]
  EqualTolerance = true
  ExtensionAngle = 0
  FormatSpec = %.2w
  FormatSpecOverTolerance = %+.2w
  FormatSpecUnderTolerance = %+.2w
  Inverted = false
  LineAngle = 0
  LockPosition = false
  MeasureType = 1
  OverTolerance = 0
  References2D = -> [ProjItem004]
  Rotation = 0
  ScaleType = 0
  TheoreticalExact = false
  Type = 0
  UnderTolerance = 0
  X = -14.8711
  Y = 31.2958
FEATURE [TechDraw::DrawViewDimension] Dimension010
  AngleOverride = false
  Arbitrary = false
  ArbitraryTolerances = false
  BoxCorners = (2) [(-57.2123,-15.649,-1e-07),(57.2123,15.649,1e-07)]
  EqualTolerance = true
  ExtensionAngle = 0
  FormatSpec = %.2w
  FormatSpecOverTolerance = %+.2w
  FormatSpecUnderTolerance = %+.2w
  Inverted = false
  LineAngle = 0
  LockPosition = false
  MeasureType = 1
  OverTolerance = 0
  References2D = -> [ProjItem001]
  Rotation = 0
  ScaleType = 0
  TheoreticalExact = false
  Type = 0
  UnderTolerance = 0
  X = 35.3336
  Y = 26.9075
FEATURE [TechDraw::DrawViewDimension] Dimension011
  AngleOverride = false
  Arbitrary = false
  ArbitraryTolerances = false
  BoxCorners = (2) [(-57.2123,-15.649,-1e-07),(57.2123,15.649,1e-07)]
  EqualTolerance = true
  ExtensionAngle = 0
  FormatSpec = %.2w
  FormatSpecOverTolerance = %+.2w
  FormatSpecUnderTolerance = %+.2w
  Inverted = false
  LineAngle = 0
  LockPosition = false
  MeasureType = 1
  OverTolerance = 0
  References2D = -> [ProjItem001]
  Rotation = 0
  ScaleType = 0
  TheoreticalExact = false
  Type = 0
  UnderTolerance = 0
  X = 17.7987
  Y = -28.1724
FEATURE [TechDraw::DrawViewDimension] Dimension012
  AngleOverride = false
  Arbitrary = false
  ArbitraryTolerances = false
  BoxCorners = (2) [(-57.2123,-15.649,-1e-07),(57.2123,15.649,1e-07)]
  EqualTolerance = true
  ExtensionAngle = 0
  FormatSpec = %.2w
  FormatSpecOverTolerance = %+.2w
  FormatSpecUnderTolerance = %+.2w
  Inverted = false
  LineAngle = 0
  LockPosition = false
  MeasureType = 1
  OverTolerance = 0
  References2D = -> [ProjItem001]
  Rotation = 0
  ScaleType = 0
  TheoreticalExact = false
  Type = 1
  UnderTolerance = 0
  X = 5.74067
  Y = -29.1155
FEATURE [TechDraw::DrawViewDimension] Dimension013
  AngleOverride = false
  Arbitrary = false
  ArbitraryTolerances = false
  BoxCorners = (2) [(-15.649,-32.4003,-1e-07),(15.649,32.4003,1e-07)]
  EqualTolerance = true
  ExtensionAngle = 0
  FormatSpec = %.2w
  FormatSpecOverTolerance = %+.2w
  FormatSpecUnderTolerance = %+.2w
  Inverted = false
  LineAngle = 0
  LockPosition = false
  MeasureType = 1
  OverTolerance = 0
  References2D = -> [ProjItem002]
  Rotation = 0
  ScaleType = 0
  TheoreticalExact = false
  Type = 0
  UnderTolerance = 0
  X = 25.2051
  Y = 43.8952
FEATURE [TechDraw::DrawPage] Page
  KeepUpdated = true
  NextBalloonIndex = 1
  ProjectionType = 0
  Template = -> Template
  Views = -> [ProjGroup,Dimension,Dimension001,Dimension002,Dimension003,Dimension004,Dimension005,Dimension006,Dimension007,Dimension008,Dimension009,Dimension010,Dimension011,Dimension012,Dimension013]
note: 1 file-system path scrubbed to <path> (originals preserved in the JSON sidecar)
